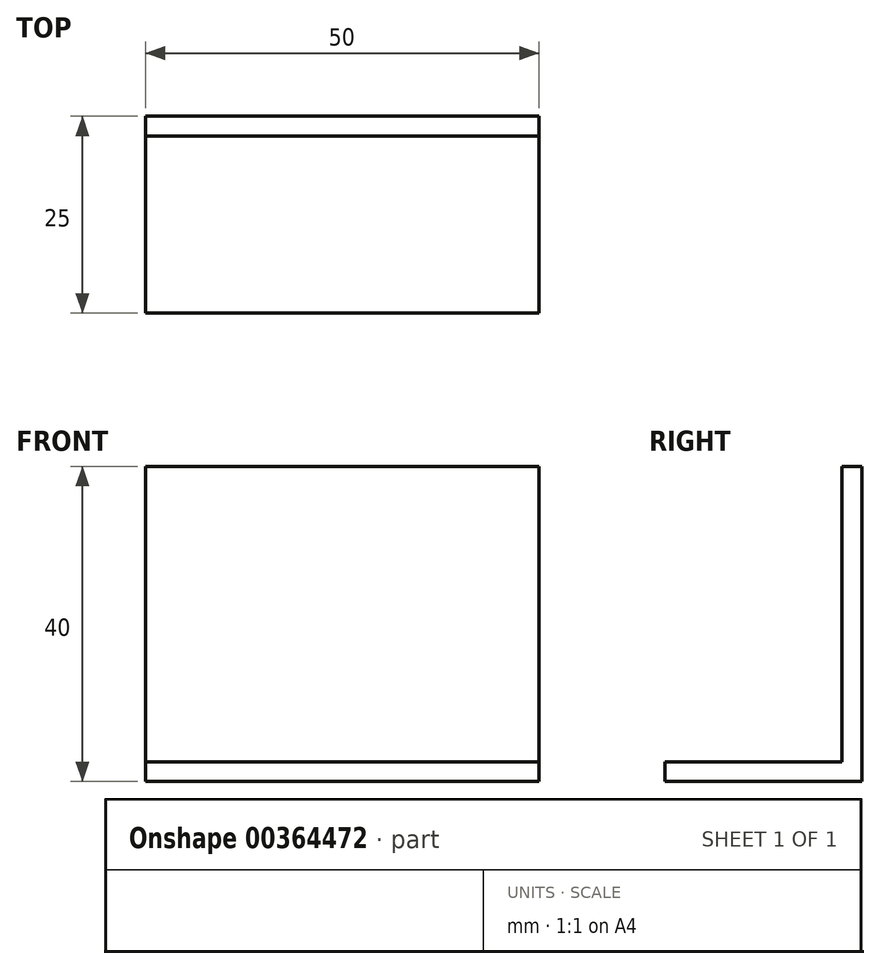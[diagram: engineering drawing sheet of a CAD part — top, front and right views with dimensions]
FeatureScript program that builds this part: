
annotation { "Feature Type Name" : "Feature", "Feature Type Description" : "" }
export const myFeature = defineFeature(function(context is Context, id is Id, definition is map)
    precondition{}
    {
        {
            var Q0;
            Q0=qCreatedBy(makeId("Front.planeOp"),FACE);
            var sketch = newSketch(context, id + "F0", { "sketchPlane" : qUnion([Q0])});
            skLineSegment(sketch, "E0", {"start": v(-25, 0) * mm, "end": v(25, 0) * mm});
            skLineSegment(sketch, "E1", {"start": v(-25, 0) * mm, "end": v(-25, 40) * mm});
            skLineSegment(sketch, "E2", {"start": v(-25, 40) * mm, "end": v(25, 40) * mm});
            skLineSegment(sketch, "E3", {"start": v(25, 40) * mm, "end": v(25, 0) * mm});
            skSolve(sketch);
        }
        {
            var Q0;
            Q0=makeQuery(id+"F0.imprint","IMPRINT",FACE,{"disambiguationData":[TD([[makeQuery(id+"F0.imprint","IMPRINT",EDGE,{"derivedFrom":sQuery(id+"F0.wireOp",EDGE,"E0")}),1.0]])]});
            extrude(context, id + "F1", {"entities" : qUnion([Q0]), "depth" : 25 * mm});
        }
        {
            var Q0;
            Q0=makeQuery(id+"F1.opExtrude","SWEPT_FACE",FACE,{"disambiguationData":[OSD([sQuery(id+"F0.wireOp",EDGE,"E2")])]});
            var Q1;
            Q1=makeQuery(id+"F1.opExtrude","CAP_FACE",FACE,{"disambiguationData":[OSD([sQuery(id+"F0.wireOp",EDGE,"E0"),sQuery(id+"F0.wireOp",EDGE,"E1"),sQuery(id+"F0.wireOp",EDGE,"E2"),sQuery(id+"F0.wireOp",EDGE,"E3")])],"isStart":false});
            var Q2;
            Q2=makeQuery(id+"F1.opExtrude","SWEPT_FACE",FACE,{"disambiguationData":[OSD([sQuery(id+"F0.wireOp",EDGE,"E3")])]});
            var Q3;
            Q3=makeQuery(id+"F1.opExtrude","SWEPT_FACE",FACE,{"disambiguationData":[OSD([sQuery(id+"F0.wireOp",EDGE,"E1")])]});
            shell(context, id + "F2", {"entities" : qUnion([Q0, Q1, Q2, Q3]), "thickness" : 2.5 * mm});
        }
    });
